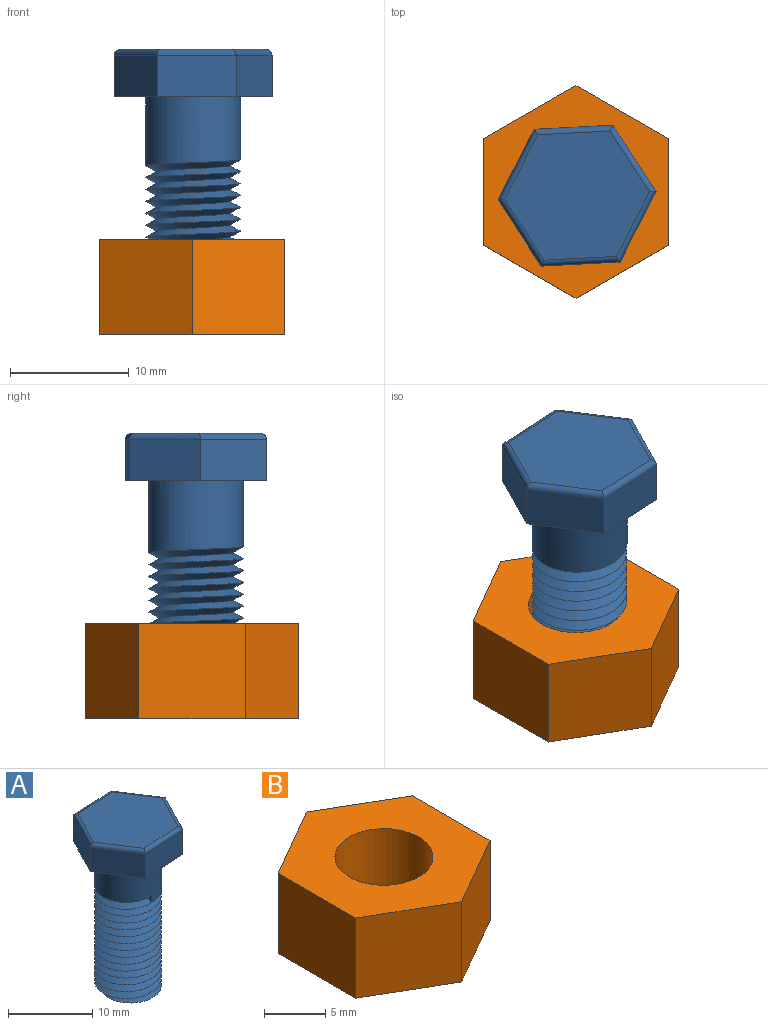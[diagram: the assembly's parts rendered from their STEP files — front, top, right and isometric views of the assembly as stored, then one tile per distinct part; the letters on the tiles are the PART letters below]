
ASSEMBLY  parts=2 mates=1
PART A: 20 faces, bbox 13.9x12.5x25.2 mm
  f0: cylinder r=4mm len=8mm, axis (0,0,-1), area 138.8mm2, adj f1,f4,f13
  f1: plane 1.02x0.9mm, normal (-1,0,0), area 0.5mm2, adj f0,f2,f3,f4
  f2: bspline ~15.5x9.17mm, area 328.9mm2, adj f1,f3,f4,f5
  f3: bspline ~15x9.17mm, area 314.5mm2, adj f1,f2,f5
  f4: bspline ~9.33x8.08mm, area 0.9mm2, adj f0,f1,f2
  f5: plane 7.74x7.73mm, normal (0,0,-1), area 39.5mm2, adj f2,f3
  f6: plane 6.65x3.52mm, normal (0.05,-1,0), area 23.4mm2, adj f7,f11,f13,f15
  f7: plane 5.93x3.52mm, normal (0.89,-0.46,0), area 23.4mm2, adj f6,f8,f13,f14
  f8: plane 5.59x3.62mm, normal (0.84,0.54,0), area 23.4mm2, adj f7,f9,f13,f16
  f9: plane 6.65x3.52mm, normal (-0.05,1,0), area 23.4mm2, adj f8,f10,f13,f18
  f10: plane 5.93x3.52mm, normal (-0.89,0.46,0), area 23.4mm2, adj f9,f11,f13,f19
  f11: plane 5.59x3.62mm, normal (-0.84,-0.54,0), area 23.4mm2, adj f6,f10,f13,f17
  f12: plane 12.18x10.86mm, normal (0,0,1), area 96.6mm2, adj f14,f15,f16,f17,f18,f19
  f13: plane 13.29x11.85mm, normal (0,0,-1), area 64.8mm2, adj f0,f6,f7,f8,f9,f10,f11
  f14: cylinder r=0.48mm len=6.15mm, axis (-0.46,-0.89,0), area 4.8mm2, adj f7,f12,f15,f16
  f15: cylinder r=0.48mm len=6.67mm, axis (-1,-0.05,0), area 4.8mm2, adj f6,f12,f14,f17
  f16: cylinder r=0.48mm len=5.85mm, axis (0.54,-0.84,0), area 4.8mm2, adj f8,f12,f14,f18
  f17: cylinder r=0.48mm len=5.85mm, axis (-0.54,0.84,0), area 4.8mm2, adj f11,f12,f15,f19
  f18: cylinder r=0.48mm len=6.67mm, axis (1,0.05,0), area 4.8mm2, adj f9,f12,f16,f19
  f19: cylinder r=0.48mm len=6.15mm, axis (0.46,0.89,0), area 4.8mm2, adj f10,f12,f17,f18
PART B: 9 faces, bbox 15.5x17.9x8 mm
  f0: plane 8x7.75mm, normal (0.5,0.87,0), area 71.6mm2, adj f1,f6,f7,f8
  f1: plane 8x7.75mm, normal (-0.5,0.87,0), area 71.6mm2, adj f0,f2,f7,f8
  f2: plane 8.95x8mm, normal (-1,0,0), area 71.6mm2, adj f1,f3,f7,f8
  f3: plane 8x7.75mm, normal (-0.5,-0.87,0), area 71.6mm2, adj f2,f4,f7,f8
  f4: plane 8x7.75mm, normal (0.5,-0.87,0), area 71.6mm2, adj f3,f6,f7,f8
  f5: cylinder r=4mm len=8mm, axis (0,0,-1), area 201.1mm2, adj f7,f8
  f6: plane 8.95x8mm, normal (1,0,0), area 71.6mm2, adj f0,f4,f7,f8
  f7: plane 17.9x15.5mm, normal (0,0,1), area 157.8mm2, adj f0,f1,f2,f3,f4,f5,f6
  f8: plane 17.9x15.5mm, normal (0,0,-1), area 157.8mm2, adj f0,f1,f2,f3,f4,f5,f6
PLACE A rot(axis=(0,0,-1),180deg) t=(-45.86,30.82,20.34)mm
PLACE B rot(axis=(0,0,1),0deg) t=(1.57,31.16,20.34)mm
MATE cylindrical A.f5 <-> B.f5  axis (0,0,-1) through (-45.95,31.16,20.34)mm
